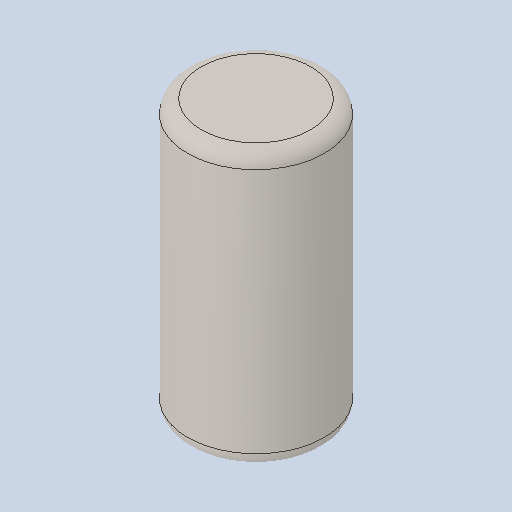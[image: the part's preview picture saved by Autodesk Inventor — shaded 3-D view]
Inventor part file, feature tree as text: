
AUTODESK INVENTOR PART (.ipt)
format: ipt  version: 2023 (Build 270158000, 158)  size: 101,376 bytes
history: native  units: in
note: dims shown in document units (in); Inventor stores cm internally (conversion verified against a paired STEP export)
features: fillet x1
ambient origin geometry x8: Origin, YZ Plane, XZ Plane, XY Plane, X Axis, Y Axis, Z Axis, Center Point
bodies: Solid1 (feature_tree)
feature tree (1):
  fillet  "Fillet1"  [1 undecoded]
note: 1 required parameter value undecoded (feature->parameter linkage not recoverable at this tier; creation-order binding heuristic only, values carry confidence <= 0.55)
